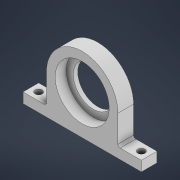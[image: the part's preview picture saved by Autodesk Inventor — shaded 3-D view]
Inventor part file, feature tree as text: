
AUTODESK INVENTOR PART (.ipt)
format: ipt  version: 2021 (Build 250183000, 183)  size: 171,008 bytes
history: native  units: mm
features: extrude x6, sketch x6, fillet x2
ambient origin geometry x8: Origin, YZ Plane, XZ Plane, XY Plane, X Axis, Y Axis, Z Axis, Center Point
bodies: Volumenkörper1 (feature_tree)
feature tree (14):
  extrude  "Extrusion1"  Depth=32.0mm
  sketch  "Skizze2"  dims[d2=24.2mm d3=7.0mm d4=0.0mm]
  extrude  "Extrusion2"  Depth=7.0mm TaperAngle=0.0deg
  extrude  "Extrusion3"  Depth=3.0mm
  extrude  "Extrusion4"  Depth=10.5mm TaperAngle=0.0deg
  fillet  "Rundung1"  Radius=24.2mm
  extrude  "Extrusion5"  Depth=2.0mm TaperAngle=0.0deg
  fillet  "Rundung2"  Radius=16.0mm
  extrude  "Extrusion6"  Depth=1.0mm
  sketch  "Skizze1"  dims[d0=32.0mm d1=32.0mm]
  sketch  "Skizze3"  dims[d5=3.0mm d6=3.0mm]
  sketch  "Skizze4"  dims[d7=10.5mm d8=0.0mm d9=10.5mm d10=0.0mm d11=24.2mm]
  sketch  "Skizze5"  dims[d12=18.0mm d13=2.0mm d14=0.0mm d15=16.0mm]
  sketch  "Skizze6"  dims[d16=3.2mm d17=3.5mm d18=3.5mm d19=3.2mm d20=3.5mm d21=3.5mm d22=5.0mm d23=0.0mm d24=1.0mm d25=3.2mm d26=3.2mm d27=1.5mm d28=0.0mm]
